# Revit family: BARPA_Norma3_LOD5
name_source: partatom
category: Electrical Equipment
revit_build: Autodesk Revit 2016 (Build: 20170117_1200(x64)
units: mm (PartAtom-declared; Revit-internal decimal feet)

## family parameters
Always vertical = Yes
Cut with Voids When Loaded = No
Part Type = Other Panel
Room Calculation Point = No
Round Connector Dimension = Use Diameter
Shared = No
Work Plane-Based = No

## types (28) — shared parameters
BARPA_Color = Black (RAL9004)
BARPA_Datasheet = https://www.barpa.eu
BARPA_Declaration of Conformity = https://www.barpa.eu
BARPA_Description = Norma cabinet was designed for Networking Rooms. It’s available in a range of heights and depths and accommodate a load of up to 800 kg.
BARPA_Earth Connection = Yes
BARPA_Instructions Manual = https://www.barpa.eu
BARPA_Instructions Video = https://www.youtube.com
BARPA_Loading Capacity = 800.00 kg
BARPA_Material = SPCC Cold Rolled Steel; 19’’ rails: 2.0mm; Casters tray: 2.0mm; Others 1.2mm
BARPA_Standard = ANSI/EIA RS-310-D; IEC60297-2; DIN41494 Part 1 and 7
IfcExportAs = IfcBuildingElementProxy
IfcExportType = DATACABINET
Manufacturer = BARPA

## per-type parameters (varying)
| type | BARPA_EAN Code | BARPA_Height | BARPA_Length | BARPA_Width | Description | Model |
| Norma 3 - 15U 600x600 | 5608445005793 | 870 mm  [stored 2.85433 ft] | 600 mm | 600 mm | Rack Norma 3 - 15U 600x600 | 82341315606 |
| Norma 3 - 15U 600x800 | 5608445005809 | 870 mm  [stored 2.85433 ft] | 800 mm  [stored 2.62467 ft] | 600 mm | Rack Norma 3 - 15U 600x800 | 82341315608 |
| Norma 3 - 20U 600x600 | 5608445005816 | 1092 mm  [stored 3.58268 ft] | 600 mm | 600 mm | Rack Norma 3 - 20U 600x600 | 82341320606 |
| Norma 3 - 20U 600x800 | 5608445005823 | 1092 mm  [stored 3.58268 ft] | 800 mm  [stored 2.62467 ft] | 600 mm | Rack Norma 3 - 20U 600x800 | 82341320608 |
| Norma 3 - 24U 600x600 | 5608445005830 | 1270 mm | 600 mm | 600 mm | Rack Norma 3 - 24U 600x600 | 82341324606 |
| Norma 3 - 24U 600x800 | 5608445005847 | 1270 mm | 800 mm  [stored 2.62467 ft] | 600 mm | Rack Norma 3 - 24U 600x800 | 82341324608 |
| Norma 3 - 29U 600x600 | 5608445005854 | 1492 mm  [stored 4.89501 ft] | 600 mm | 600 mm | Rack Norma 3 - 29U 600x600 | 82341329606 |
| Norma 3 - 29U 600x800 | 5608445005861 | 1492 mm  [stored 4.89501 ft] | 800 mm  [stored 2.62467 ft] | 600 mm | Rack Norma 3 - 29U 600x800 | 82341329608 |
| Norma 3 - 33U 600x600 | 5608445005878 | 1670 mm | 600 mm | 600 mm | Rack Norma 3 - 33U 600x600 | 82341333606 |
| Norma 3 - 33U 600x800 | 5608445005885 | 1670 mm | 800 mm  [stored 2.62467 ft] | 600 mm | Rack Norma 3 - 33U 600x800 | 82341333608 |
| Norma 3 - 38U 600x600 | 5608445005892 | 1892 mm  [stored 6.20735 ft] | 600 mm | 600 mm | Rack Norma 3 - 38U 600x600 | 82341338606 |
| Norma 3 - 38U 600x800 | 5608445005908 | 1892 mm  [stored 6.20735 ft] | 800 mm  [stored 2.62467 ft] | 600 mm | Rack Norma 3 - 38U 600x800 | 82341338608 |
| Norma 3 - 38U 600x1000 | 5608445005915 | 1892 mm  [stored 6.20735 ft] | 1000 mm  [stored 3.28084 ft] | 600 mm | Rack Norma 3 - 38U 600x1000 | 82341338610 |
| Norma 3 - 38U 800x600 | 5608445005922 | 1892 mm  [stored 6.20735 ft] | 600 mm | 800 mm  [stored 2.62467 ft] | Rack Norma 3 - 38U 800x600 | 82341338806 |
| Norma 3 - 38U 800x800 | 5608445005939 | 1892 mm  [stored 6.20735 ft] | 800 mm  [stored 2.62467 ft] | 800 mm  [stored 2.62467 ft] | Rack Norma 3 - 38U 800x800 | 82341338808 |
| Norma 3 - 38U 800x1000 | 5608445005946 | 1892 mm  [stored 6.20735 ft] | 1000 mm  [stored 3.28084 ft] | 800 mm  [stored 2.62467 ft] | Rack Norma 3 - 38U 800x1000 | 82341338810 |
| Norma 3 - 42U 600x600 | 5608445005953 | 2070 mm  [stored 6.79134 ft] | 600 mm | 600 mm | Rack Norma 3 - 42U 600x600 | 82341342606 |
| Norma 3 - 42U 600x800 | 5608445005960 | 2070 mm  [stored 6.79134 ft] | 800 mm  [stored 2.62467 ft] | 600 mm | Rack Norma 3 - 42U 600x800 | 82341342608 |
| Norma 3 - 42U 600x1000 | 5608445005977 | 2070 mm  [stored 6.79134 ft] | 1000 mm  [stored 3.28084 ft] | 600 mm | Rack Norma 3 - 42U 600x1000 | 82341342610 |
| Norma 3 - 42U 800x600 | 5608445005984 | 2070 mm  [stored 6.79134 ft] | 600 mm | 800 mm  [stored 2.62467 ft] | Rack Norma 3 - 42U 800x600 | 82341342806 |
| Norma 3 - 42U 800x800 | 5608445005991 | 2070 mm  [stored 6.79134 ft] | 800 mm  [stored 2.62467 ft] | 800 mm  [stored 2.62467 ft] | Rack Norma 3 - 42U 800x800 | 82341342808 |
| Norma 3 - 42U 800x1000 | 5608445006004 | 2070 mm  [stored 6.79134 ft] | 1000 mm  [stored 3.28084 ft] | 800 mm  [stored 2.62467 ft] | Rack Norma 3 - 42U 800x1000 | 82341342810 |
| Norma 3 - 47U 600x600 | 5608445006011 | 2292 mm  [stored 7.51969 ft] | 600 mm | 600 mm | Rack Norma 3 - 47U 600x600 | 82341347606 |
| Norma 3 - 47U 600x800 | 5608445006028 | 2292 mm  [stored 7.51969 ft] | 800 mm  [stored 2.62467 ft] | 600 mm | Rack Norma 3 - 47U 600x800 | 82341347608 |
| Norma 3 - 47U 600x1000 | 5608445006035 | 2292 mm  [stored 7.51969 ft] | 1000 mm  [stored 3.28084 ft] | 600 mm | Rack Norma 3 - 47U 600x1000 | 82341347610 |
| Norma 3 - 47U 800x600 | 5608445006042 | 2292 mm  [stored 7.51969 ft] | 600 mm | 800 mm  [stored 2.62467 ft] | Rack Norma 3 - 47U 800x600 | 82341347806 |
| Norma 3 - 47U 800x800 | 5608445006059 | 2292 mm  [stored 7.51969 ft] | 800 mm  [stored 2.62467 ft] | 800 mm  [stored 2.62467 ft] | Rack Norma 3 - 47U 800x800 | 82341347808 |
| Norma 3 - 47U 800x1000 | 5608445006066 | 2292 mm  [stored 7.51969 ft] | 1000 mm  [stored 3.28084 ft] | 800 mm  [stored 2.62467 ft] | Rack Norma 3 - 47U 800x1000 | 82341347810 |

note: [stored X ft] marks values corroborated as IEEE doubles in the binary element streams (Revit-internal decimal feet)

## geometry (parser evidence)
native form markers: Sweep x16
no freeform markers — native parametric forms only
